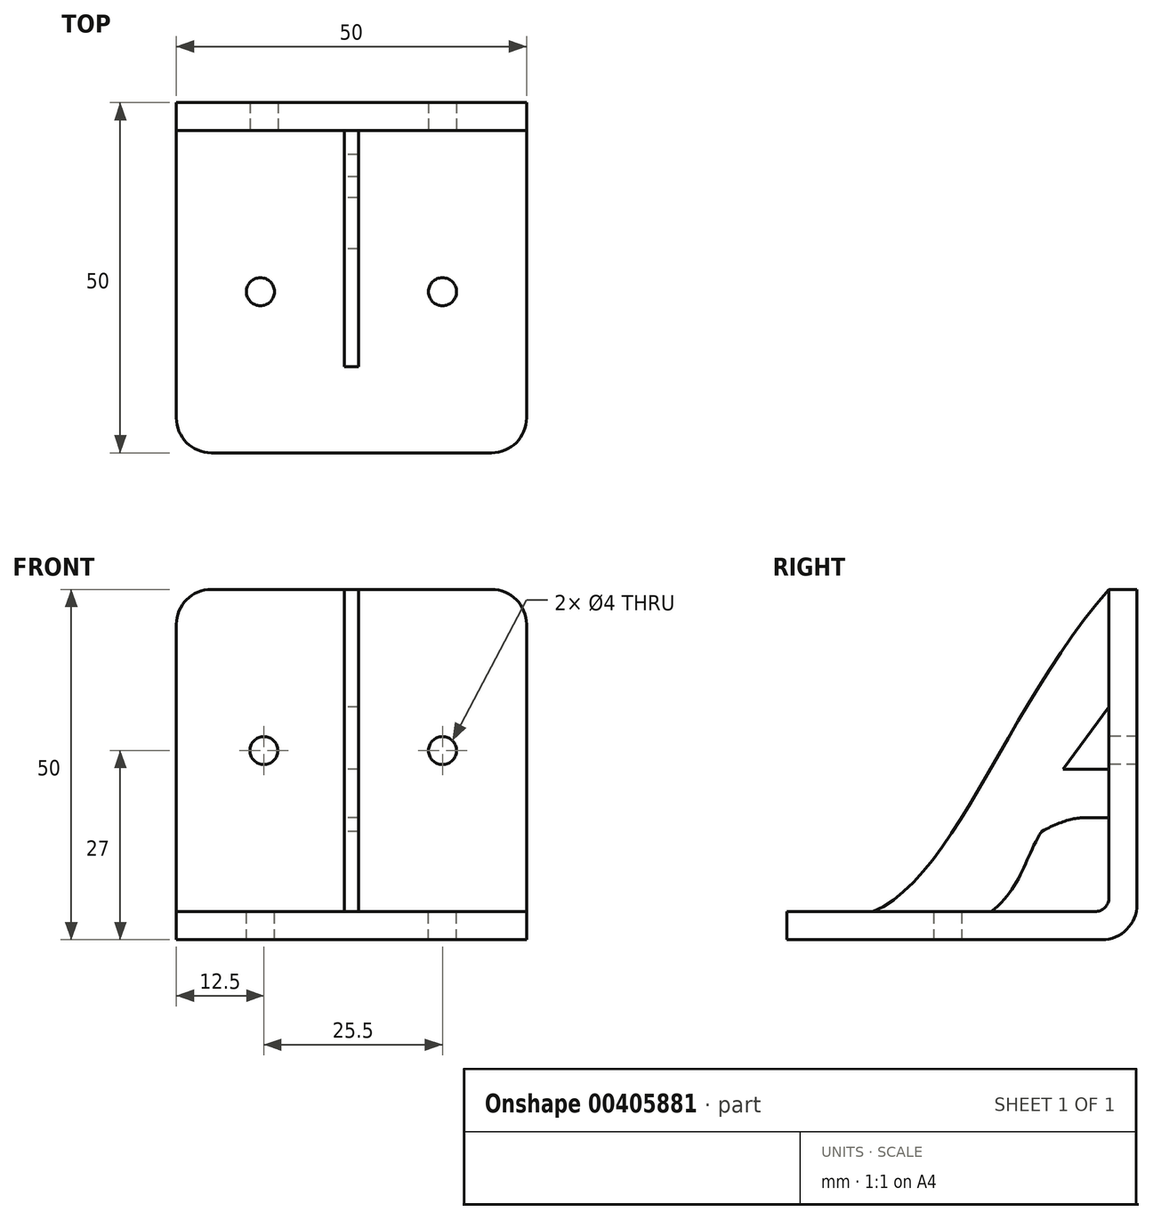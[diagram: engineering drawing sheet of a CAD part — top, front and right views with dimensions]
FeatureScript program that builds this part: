
annotation { "Feature Type Name" : "Feature", "Feature Type Description" : "" }
export const myFeature = defineFeature(function(context is Context, id is Id, definition is map)
    precondition{}
    {
        {
            var Q0;
            Q0=qCreatedBy(makeId("Right.planeOp"),FACE);
            var sketch = newSketch(context, id + "F0", { "sketchPlane" : qUnion([Q0])});
            skLineSegment(sketch, "E0", {"start": v(-50, 0) * mm, "end": v(0, 0) * mm});
            skLineSegment(sketch, "E1", {"start": v(0, 0) * mm, "end": v(0, 50) * mm});
            skLineSegment(sketch, "E2", {"start": v(0, 50) * mm, "end": v(-4, 50) * mm});
            skLineSegment(sketch, "E3", {"start": v(-4, 50) * mm, "end": v(-4, 4) * mm});
            skLineSegment(sketch, "E4", {"start": v(-4, 4) * mm, "end": v(-50, 4) * mm});
            skLineSegment(sketch, "E5", {"start": v(-50, 4) * mm, "end": v(-50, 0) * mm});
            skSolve(sketch);
        }
        {
            var Q0;
            Q0=makeQuery(id+"F0.imprint","IMPRINT",FACE,{"disambiguationData":[TD([[makeQuery(id+"F0.imprint","IMPRINT",EDGE,{"derivedFrom":sQuery(id+"F0.wireOp",EDGE,"E0")}),1.0]])]});
            extrude(context, id + "F1", {"entities" : qUnion([Q0]), "depth" : 50 * mm});
        }
        {
            var Q0;
            Q0=makeQuery(id+"F1.opExtrude","SWEPT_FACE",FACE,{"disambiguationData":[OSD([sQuery(id+"F0.wireOp",EDGE,"E3")])]});
            var sketch = newSketch(context, id + "F2", { "sketchPlane" : qUnion([Q0])});
            skLineSegment(sketch, "E6", {"start": v(24, 50) * mm, "end": v(24, 4) * mm});
            skLineSegment(sketch, "E7", {"start": v(25, 50) * mm, "end": v(24, 50) * mm});
            skLineSegment(sketch, "E8", {"start": v(25, 50) * mm, "end": v(26, 50) * mm});
            skLineSegment(sketch, "E9", {"start": v(26, 50) * mm, "end": v(26, 4) * mm});
            skLineSegment(sketch, "E10", {"start": v(26, 4) * mm, "end": v(24, 4) * mm});
            skLineSegment(sketch, "E11", {"start": v(24, 50) * mm, "end": v(26, 50) * mm});
            skSolve(sketch);
        }
        {
            var Q0;
            Q0 = qSketchRegion(id + "F2", true);
            extrude(context, id + "F3", {"entities" : qUnion([Q0]), "operationType" : NewBodyOperationType.ADD, "depth" : 46 * mm});
        }
        {
            var Q0;
            Q0=makeQuery(id+"F3.opExtrude","SWEPT_FACE",FACE,{"disambiguationData":[OSD([sQuery(id+"F2.wireOp",EDGE,"E6")])]});
            var sketch = newSketch(context, id + "F4", { "sketchPlane" : qUnion([Q0])});
            skFitSpline(sketch, "E12", {"points": [v(4, 50) * mm, v(37.73, 4) * mm, v(49.37, 4) * mm], "startDerivative": vector(61.97, -69.5) * mm, "endDerivative": vector(2.73, 1.2) * mm});
            skSolve(sketch);
        }
        {
            var Q0;
            {var subQ0=sQuery(id+"F2.wireOp",EDGE,"E6");var subQ3=makeQuery(id+"F3.opExtrude","CAP_EDGE",EDGE,{"disambiguationData":[OSD([subQ0])],"isStart":false});Q0=makeQuery(id+"F4.imprint","IMPRINT",FACE,{"disambiguationData":[TD([[makeQuery(id+"F4.imprint","IMPRINT",EDGE,{"derivedFrom":subQ3}),-1.0]])]});}
            extrude(context, id + "F5", {"entities" : qUnion([Q0]), "operationType" : NewBodyOperationType.REMOVE, "oppositeDirection" : true, "depth" : 25 * mm});
        }
        {
            var Q0;
            Q0=makeQuery(id+"F3.opExtrude","SWEPT_FACE",FACE,{"disambiguationData":[OSD([sQuery(id+"F2.wireOp",EDGE,"E6")])]});
            var sketch = newSketch(context, id + "F6", { "sketchPlane" : qUnion([Q0])});
            skFitSpline(sketch, "E13", {"points": [v(20.86, 4) * mm, v(13.6, 15.47) * mm], "startDerivative": vector(-12.77, 9.4) * mm, "endDerivative": vector(-7.27, 11.11) * mm});
            skFitSpline(sketch, "E14", {"points": [v(13.6, 15.47) * mm, v(4, 15.47) * mm], "startDerivative": vector(-14.9, 7.98) * mm, "endDerivative": vector(-4.82, -7.45) * mm});
            skLineSegment(sketch, "E15", {"start": v(4, 33.2) * mm, "end": v(10.57, 24.34) * mm});
            skLineSegment(sketch, "E16", {"start": v(10.57, 24.34) * mm, "end": v(4, 24.34) * mm});
            skSolve(sketch);
        }
        {
            var Q0;
            {var subQ0=sQuery(id+"F6.wireOp",EDGE,"E13");Q0=makeQuery(id+"F6.imprint","IMPRINT",FACE,{"disambiguationData":[TD([[makeQuery(id+"F6.imprint","IMPRINT",EDGE,{"derivedFrom":subQ0}),1.0]])]});}
            var Q1;
            {var subQ0=sQuery(id+"F6.wireOp",EDGE,"E15");Q1=makeQuery(id+"F6.imprint","IMPRINT",FACE,{"disambiguationData":[TD([[makeQuery(id+"F6.imprint","IMPRINT",EDGE,{"derivedFrom":subQ0}),-1.0]])]});}
            extrude(context, id + "F7", {"entities" : qUnion([Q0, Q1]), "operationType" : NewBodyOperationType.REMOVE, "oppositeDirection" : true, "depth" : 25 * mm});
        }
        {
            var Q0;
            Q0=makeQuery(id+"F3.opExtrude","SWEPT_FACE",FACE,{"disambiguationData":[OSD([sQuery(id+"F2.wireOp",EDGE,"E6")])]});
            var sketch = newSketch(context, id + "F8", { "sketchPlane" : qUnion([Q0])});
            skLineSegment(sketch, "E17", {"start": v(7.43, 17.4) * mm, "end": v(4, 17.4) * mm});
            skLineSegment(sketch, "E18", {"start": v(4, 17.4) * mm, "end": v(4, 15.47) * mm});
            skLineSegment(sketch, "E19", {"start": v(4, 15.47) * mm, "end": v(7.43, 15.47) * mm});
            skLineSegment(sketch, "E20", {"start": v(7.43, 15.47) * mm, "end": v(7.43, 17.4) * mm});
            skSolve(sketch);
        }
        {
            var Q0;
            Q0 = qSketchRegion(id + "F8", true);
            extrude(context, id + "F9", {"entities" : qUnion([Q0]), "operationType" : NewBodyOperationType.REMOVE, "oppositeDirection" : true, "depth" : 25 * mm});
        }
        {
            var Q0;
            {var subQ0=sQuery(id+"F2.wireOp",EDGE,"E6");var subQ1=makeQuery(id+"F3.opExtrude","CAP_EDGE",EDGE,{"disambiguationData":[OSD([subQ0])],"isStart":true});var subQ3=sQuery(id+"F0.wireOp",EDGE,"E3");var subQ11=makeQuery(id+"F1.opExtrude","SWEPT_FACE",FACE,{"disambiguationData":[OSD([subQ3])]});Q0=makeQuery(id+"F9.boolean.opBoolean","MERGE",FACE,{"derivedFrom":[makeQuery(id+"F7.boolean.opBoolean","MERGE",FACE,{"derivedFrom":[makeQuery(id+"F3.boolean.opBoolean","SPLIT",FACE,{"disambiguationData":[TD([makeQuery(id+"F3.opExtrude","SWEPT_FACE",FACE,{"disambiguationData":[OSD([subQ0])]})])],"derivedFrom":subQ11}),makeQuery(id+"F3.boolean.opBoolean","SPLIT",FACE,{"disambiguationData":[TD([makeQuery(id+"F3.opExtrude","SWEPT_FACE",FACE,{"disambiguationData":[OSD([sQuery(id+"F2.wireOp",EDGE,"E9")])]})])],"derivedFrom":subQ11}),makeQuery(id+"F7.opExtrude","SWEPT_FACE",FACE,{"disambiguationData":[OSD([subQ0]),TDD([makeQuery(id+"F6.imprint","IMPRINT",EDGE,{"disambiguationData":[TD([[makeQuery(id+"F6.imprint","INTERSECT",VERTEX,{"derivedFrom":[subQ1,sQuery(id+"F6.wireOp",EDGE,"E14")]}),-1.0]])],"derivedFrom":subQ1})])]}),makeQuery(id+"F7.opExtrude","SWEPT_FACE",FACE,{"disambiguationData":[OSD([subQ0]),TDD([makeQuery(id+"F6.imprint","IMPRINT",EDGE,{"disambiguationData":[TD([[makeQuery(id+"F6.imprint","INTERSECT",VERTEX,{"derivedFrom":[subQ1,sQuery(id+"F6.wireOp",EDGE,"E15")]}),-1.0]])],"derivedFrom":subQ1})])]})]}),makeQuery(id+"F9.opExtrude","SWEPT_FACE",FACE,{"disambiguationData":[OSD([sQuery(id+"F8.wireOp",EDGE,"E18")])]})]});}
            var sketch = newSketch(context, id + "F10", { "sketchPlane" : qUnion([Q0])});
            skLineSegment(sketch, "E21", {"start": v(25, 4) * mm, "end": v(0, 4) * mm});
            skLineSegment(sketch, "E22", {"start": v(50, 4) * mm, "end": v(26, 4) * mm});
            skCircle(sketch, "E23", {"center": v(38, 27) * mm, "radius": 4.06 * mm});
            skCircle(sketch, "E24", {"center": v(12.5, 27) * mm, "radius": 4.38 * mm});
            skSolve(sketch);
        }
        {
            var Q0;
            {var subQ0=sQuery(id+"F2.wireOp",EDGE,"E10");var subQ1=sQuery(id+"F2.wireOp",EDGE,"E6");var subQ2=sQuery(id+"F0.wireOp",EDGE,"E4");var subQ3=sQuery(id+"F0.wireOp",EDGE,"E3");var subQ4=sQuery(id+"F2.wireOp",EDGE,"E9");var subQ12=makeQuery(id+"F1.opExtrude","SWEPT_FACE",FACE,{"disambiguationData":[OSD([subQ2])]});Q0=makeQuery(id+"F7.boolean.opBoolean","MERGE",FACE,{"derivedFrom":[makeQuery(id+"F5.boolean.opBoolean","MERGE",FACE,{"derivedFrom":[makeQuery(id+"F3.boolean.opBoolean","SPLIT",FACE,{"disambiguationData":[TD([makeQuery(id+"F3.opExtrude","SWEPT_FACE",FACE,{"disambiguationData":[OSD([subQ1])]})])],"derivedFrom":subQ12}),makeQuery(id+"F3.boolean.opBoolean","SPLIT",FACE,{"disambiguationData":[TD([makeQuery(id+"F3.opExtrude","SWEPT_FACE",FACE,{"disambiguationData":[OSD([subQ4])]})])],"derivedFrom":subQ12}),makeQuery(id+"F5.opExtrude","SWEPT_FACE",FACE,{"disambiguationData":[OSD([subQ3,subQ2,subQ1,subQ0])]})]}),makeQuery(id+"F7.opExtrude","SWEPT_FACE",FACE,{"disambiguationData":[OSD([subQ3,subQ2,subQ1,subQ0])]})]});}
            var sketch = newSketch(context, id + "F11", { "sketchPlane" : qUnion([Q0])});
            skLineSegment(sketch, "E25", {"start": v(0, -4) * mm, "end": v(24, -4) * mm});
            skLineSegment(sketch, "E26", {"start": v(50, -4) * mm, "end": v(50, -50) * mm});
            skLineSegment(sketch, "E27", {"start": v(26, -4) * mm, "end": v(50, -4) * mm});
            skCircle(sketch, "E28", {"center": v(12, -27) * mm, "radius": 5.15 * mm});
            skCircle(sketch, "E29", {"center": v(38, -27) * mm, "radius": 5.2 * mm});
            skSolve(sketch);
        }
        {
            var Q0;
            Q0=sQuery(id+"F10.wireOp",VERTEX,"E24.center");
            var Q1;
            Q1=sQuery(id+"F10.wireOp",VERTEX,"E23.center");
            var Q2;
            Q2=sQuery(id+"F11.wireOp",VERTEX,"E29.center");
            var Q3;
            Q3=sQuery(id+"F11.wireOp",VERTEX,"E28.center");
            var Q4;
            Q4=makeQuery(id+"F1.opExtrude","SWEPT_BODY",BODY,{"disambiguationData":[OSD([sQuery(id+"F0.wireOp",EDGE,"E0"),sQuery(id+"F0.wireOp",EDGE,"E1"),sQuery(id+"F0.wireOp",EDGE,"E2"),sQuery(id+"F0.wireOp",EDGE,"E3"),sQuery(id+"F0.wireOp",EDGE,"E4"),sQuery(id+"F0.wireOp",EDGE,"E5")])]});
            hole(context, id + "F12", {"style" : HoleStyle.SIMPLE, "endStyle" : HoleEndStyle.BLIND, "holeDiameter" : 4 * mm, "holeDepth" : 16 * mm, "isTappedThrough" : true, "tappedDepth" : 12.7 * mm, "tapClearance" : 3, "locations" : qUnion([Q0, Q1, Q2, Q3]), "scope" : qUnion([Q4])});
        }
        {
            var Q0;
            Q0=makeQuery(id+"F1.opExtrude","SWEPT_EDGE",EDGE,{"disambiguationData":[OSD([sQuery(id+"F0.wireOp",EDGE,"E0"),sQuery(id+"F0.wireOp",EDGE,"E1")])]});
            fillet(context, id + "F13", {"entities" : qUnion([Q0]), "radius" : 5 * mm, "tangentPropagation" : true, "allowEdgeOverflow" : false});
        }
        {
            var Q0;
            {var subQ0=sQuery(id+"F2.wireOp",EDGE,"E6");var subQ1=sQuery(id+"F0.wireOp",EDGE,"E4");var subQ2=sQuery(id+"F0.wireOp",EDGE,"E3");var subQ9=makeQuery(id+"F1.opExtrude","SWEPT_EDGE",EDGE,{"disambiguationData":[OSD([subQ2,subQ1])]});Q0=makeQuery(id+"F7.boolean.opBoolean","MERGE",EDGE,{"derivedFrom":[makeQuery(id+"F3.boolean.opBoolean","SPLIT",EDGE,{"disambiguationData":[TD([makeQuery(id+"F3.opExtrude","SWEPT_FACE",FACE,{"disambiguationData":[OSD([subQ0])]})])],"derivedFrom":subQ9}),makeQuery(id+"F3.boolean.opBoolean","SPLIT",EDGE,{"disambiguationData":[TD([makeQuery(id+"F3.opExtrude","SWEPT_FACE",FACE,{"disambiguationData":[OSD([sQuery(id+"F2.wireOp",EDGE,"E9")])]})])],"derivedFrom":subQ9}),makeQuery(id+"F7.opExtrude","SWEPT_EDGE",EDGE,{"disambiguationData":[OSD([subQ2,subQ1,subQ0,sQuery(id+"F2.wireOp",EDGE,"E10")])]})]});}
            fillet(context, id + "F14", {"entities" : qUnion([Q0]), "radius" : 2 * mm, "tangentPropagation" : true, "allowEdgeOverflow" : false});
        }
        {
            var Q0;
            Q0=makeQuery(id+"F1.opExtrude","CAP_EDGE",EDGE,{"disambiguationData":[OSD([sQuery(id+"F0.wireOp",EDGE,"E2")])],"isStart":true});
            var Q1;
            Q1=makeQuery(id+"F1.opExtrude","CAP_EDGE",EDGE,{"disambiguationData":[OSD([sQuery(id+"F0.wireOp",EDGE,"E2")])],"isStart":false});
            var Q2;
            Q2=makeQuery(id+"F1.opExtrude","CAP_EDGE",EDGE,{"disambiguationData":[OSD([sQuery(id+"F0.wireOp",EDGE,"E5")])],"isStart":true});
            var Q3;
            Q3=makeQuery(id+"F1.opExtrude","CAP_EDGE",EDGE,{"disambiguationData":[OSD([sQuery(id+"F0.wireOp",EDGE,"E5")])],"isStart":false});
            fillet(context, id + "F15", {"entities" : qUnion([Q0, Q1, Q2, Q3]), "radius" : 5 * mm, "tangentPropagation" : true, "allowEdgeOverflow" : false});
        }
    });
